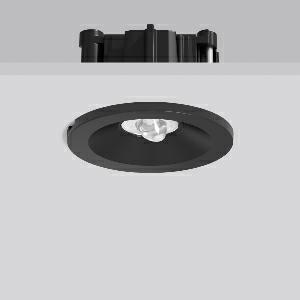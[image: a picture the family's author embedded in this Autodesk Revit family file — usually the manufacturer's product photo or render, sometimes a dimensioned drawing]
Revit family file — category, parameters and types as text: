
# Revit family: turia_l_672561_003_07_74c3
name_source: partatom
category: Lighting Fixtures
units: mm (PartAtom-declared; Revit-internal decimal feet)

## family parameters
Cut with Voids When Loaded = No
Host = Face
Light Source = No
Part Type = Normal
Room Calculation Point = No
Round Connector Dimension = Use Diameter
Shared = No

## types (1)
- TURIA L (1 x LED Modul 765, 240 lm, 6500)
    Apparent Load = 4 VA
    CIE Flux Codes = 70 91 99 100 100
    Color Rendering = 70
    Color Temperature = 6500
    Default Elevation = 1800 mm
    Description = Series: TURIA L
Round emergency luminaire for escape route lighting. Housing: die-cast aluminium. Bezel ring: plastic. With asymmetrical beam plastic lenses for illuminating rescue facilities. Self-contained system with automatic self-test and feedback via DALI bus, only to RZB DALI monitoring system. With enclosed separate ceiling mounting ring also suitable for ceiling cut-outs of Ø 68 mm. 
Colour: black
Diameter: 62 mm
Height: 3 mm
Cut-out diameter: 54-68 mm
Recess height: 76-162 mm
Luminaire: recess height: 42 mm
Weight: 430 g
Operating mode: non-maintained power mode
Duration time: 3 h
Lamp: LED
Socket: without socket
Colour temperature: 6500K
Colour rendering index (CRI): 70
System power: 4.2 W
Rated luminous flux: 240 lm
Luminous flux, emergency: 170 lm
System power, emergency: -
Control gear: Regulated power supply
Protection class: II
Type of protection: IP 20
    Height = 0 mm  [stored 0 ft]
    Lamp = 1 x LED Modul 765
    Lamp Light Flux = 240 lm
    Lamp count = 1
    Length = 62 mm  [stored 0.203412 ft]
    Lifetime = 50000 h
    Luminous efficacy = 57 lm/W
    Manufacturer = RZB
    ModVariant = No
    Model = 672561.003.07
    Mounting Place = Ceiling
    Mounting Type = Recessed
    Number of Poles = 1
    OnlyDefault = Yes
    Power Factor = 1
    Product Name = TURIA L
    Product group = Recessed ceiling luminaires
    ProductGroupID = 405
    Protection Class = Protection class II
    Protection Degree = IP 20
    RLX_Detail_Level = 1
    RLX_Emergency_Light_Flux = 170 lm
    RLX_Emergency_Type = 3
    RLX_Emergency_Type_DB = Yes
    RlxData = <blob elided: 58197 chars, md5=011e2452>
    Socket = socket
    Standby Power = 0 W
    System Light Flux = 240 lm
    System Power = 4 W
    Type Comments = Product without accessories
    Type Image = 672561.003.jpg
    URL = http://relux.com
    VarID = ---
    Voltage = 230 V
    Voltage Range = 220-240 V
    Weight = 0.00 kg
    Width = 0 mm  [stored 0 ft]

note: [stored X ft] marks values corroborated as IEEE doubles in the binary element streams (Revit-internal decimal feet)

## geometry (parser evidence)
native form markers: Blend x4, Sweep x13
no freeform markers — native parametric forms only
